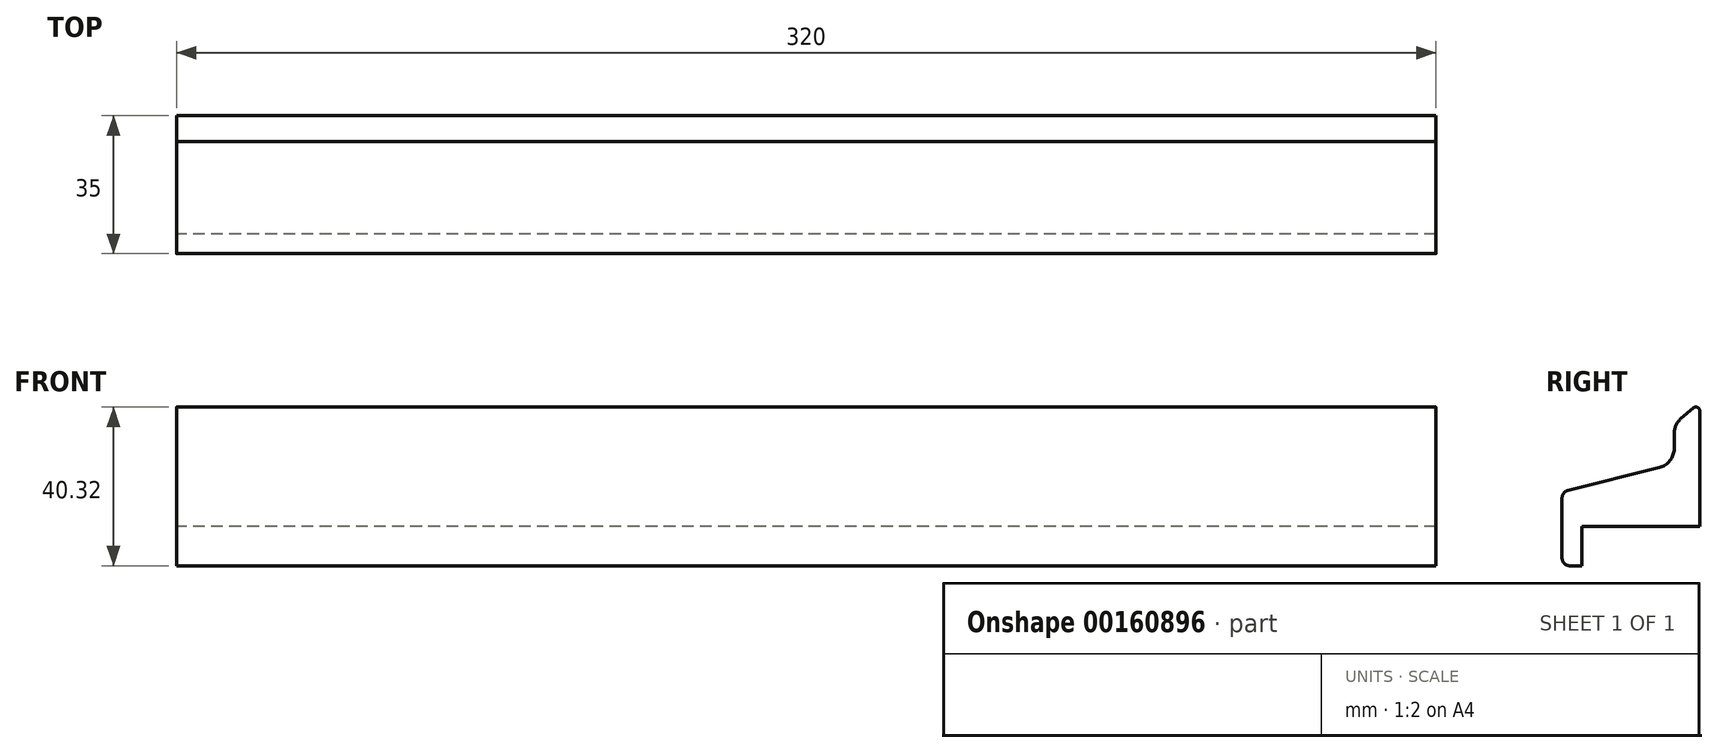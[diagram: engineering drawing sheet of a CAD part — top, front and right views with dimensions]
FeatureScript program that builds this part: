
annotation { "Feature Type Name" : "Feature", "Feature Type Description" : "" }
export const myFeature = defineFeature(function(context is Context, id is Id, definition is map)
    precondition{}
    {
        {
            var Q0;
            Q0=qCreatedBy(makeId("Front.planeOp"),FACE);
            var sketch = newSketch(context, id + "F0", { "sketchPlane" : qUnion([Q0])});
            skLineSegment(sketch, "E0.bottom", {"start": v(160, -37.5) * mm, "end": v(-160, -37.5) * mm, "construction": true});
            skLineSegment(sketch, "E0.top", {"start": v(160, 37.5) * mm, "end": v(-160, 37.5) * mm, "construction": true});
            skLineSegment(sketch, "E0.left", {"start": v(160, -37.5) * mm, "end": v(160, 37.5) * mm, "construction": true});
            skLineSegment(sketch, "E0.right", {"start": v(-160, -37.5) * mm, "end": v(-160, 37.5) * mm, "construction": true});
            skPoint(sketch, "E0.middle", {"position": v(0, 0) * mm});
            skLineSegment(sketch, "E1.bottom", {"start": v(150, -27.5) * mm, "end": v(-150, -27.5) * mm});
            skLineSegment(sketch, "E1.top", {"start": v(150, 27.5) * mm, "end": v(-150, 27.5) * mm});
            skLineSegment(sketch, "E1.left", {"start": v(150, -27.5) * mm, "end": v(150, 27.5) * mm});
            skLineSegment(sketch, "E1.right", {"start": v(-150, -27.5) * mm, "end": v(-150, 27.5) * mm});
            skLineSegment(sketch, "E2.bottom", {"start": v(187.05, -56.97) * mm, "end": v(-187.05, -56.97) * mm});
            skLineSegment(sketch, "E2.top", {"start": v(187.05, 56.97) * mm, "end": v(-187.05, 56.97) * mm});
            skLineSegment(sketch, "E2.left", {"start": v(187.05, -56.97) * mm, "end": v(187.05, 56.97) * mm});
            skLineSegment(sketch, "E2.right", {"start": v(-187.05, -56.97) * mm, "end": v(-187.05, 56.97) * mm});
            skSolve(sketch);
        }
        {
            var Q0;
            Q0=qCreatedBy(makeId("Right.planeOp"),FACE);
            var sketch = newSketch(context, id + "F1", { "sketchPlane" : qUnion([Q0])});
            skLineSegment(sketch, "E3", {"start": v(-3.48, -28.37) * mm, "end": v(19.7, -22.59) * mm});
            skLineSegment(sketch, "E4", {"start": v(-5, -30.3) * mm, "end": v(-5, -45.5) * mm});
            skLineSegment(sketch, "E5", {"start": v(-3, -47.5) * mm, "end": v(0, -47.5) * mm});
            skLineSegment(sketch, "E6", {"start": v(23.5, -17.73) * mm, "end": v(23.5, -13.92) * mm});
            skLineSegment(sketch, "E7", {"start": v(25.22, -10.15) * mm, "end": v(28.34, -7.43) * mm});
            skLineSegment(sketch, "E8", {"start": v(30, -8.18) * mm, "end": v(30, -37.5) * mm});
            skLineSegment(sketch, "E9", {"start": v(30, -37.5) * mm, "end": v(0, -37.5) * mm});
            skLineSegment(sketch, "E10", {"start": v(0, -37.5) * mm, "end": v(0, -47.5) * mm});
            skPoint(sketch, "E11.visualSharp", {"position": v(23.5, -21.64) * mm});
            skArc(sketch, "E11.filletArc", {"start": v(19.7, -22.59) * mm, "mid": v(22.44, -20.81) * mm, "end": v(23.5, -17.73) * mm});
            skPoint(sketch, "E12.visualSharp", {"position": v(23.5, -11.64) * mm});
            skArc(sketch, "E12.filletArc", {"start": v(25.22, -10.15) * mm, "mid": v(23.95, -11.85) * mm, "end": v(23.5, -13.92) * mm});
            skPoint(sketch, "E13.visualSharp", {"position": v(30, -6) * mm});
            skArc(sketch, "E13.filletArc", {"start": v(30, -8.18) * mm, "mid": v(29.41, -7.27) * mm, "end": v(28.34, -7.43) * mm});
            skPoint(sketch, "E14.visualSharp", {"position": v(-5, -28.75) * mm});
            skArc(sketch, "E14.filletArc", {"start": v(-3.48, -28.37) * mm, "mid": v(-4.58, -29.08) * mm, "end": v(-5, -30.3) * mm});
            skPoint(sketch, "E15.visualSharp", {"position": v(-5, -47.5) * mm});
            skArc(sketch, "E15.filletArc", {"start": v(-5, -45.5) * mm, "mid": v(-4.41, -46.91) * mm, "end": v(-3, -47.5) * mm});
            skSolve(sketch);
        }
        {
            var Q0;
            Q0=makeQuery(id+"F1.imprint","IMPRINT",FACE,{"disambiguationData":[TD([[makeQuery(id+"F1.imprint","IMPRINT",EDGE,{"derivedFrom":sQuery(id+"F1.wireOp",EDGE,"E3")}),-1.0]])]});
            extrude(context, id + "F2", {"entities" : qUnion([Q0]), "endBound" : BoundingType.SYMMETRIC, "depth" : 320 * mm});
        }
    });
